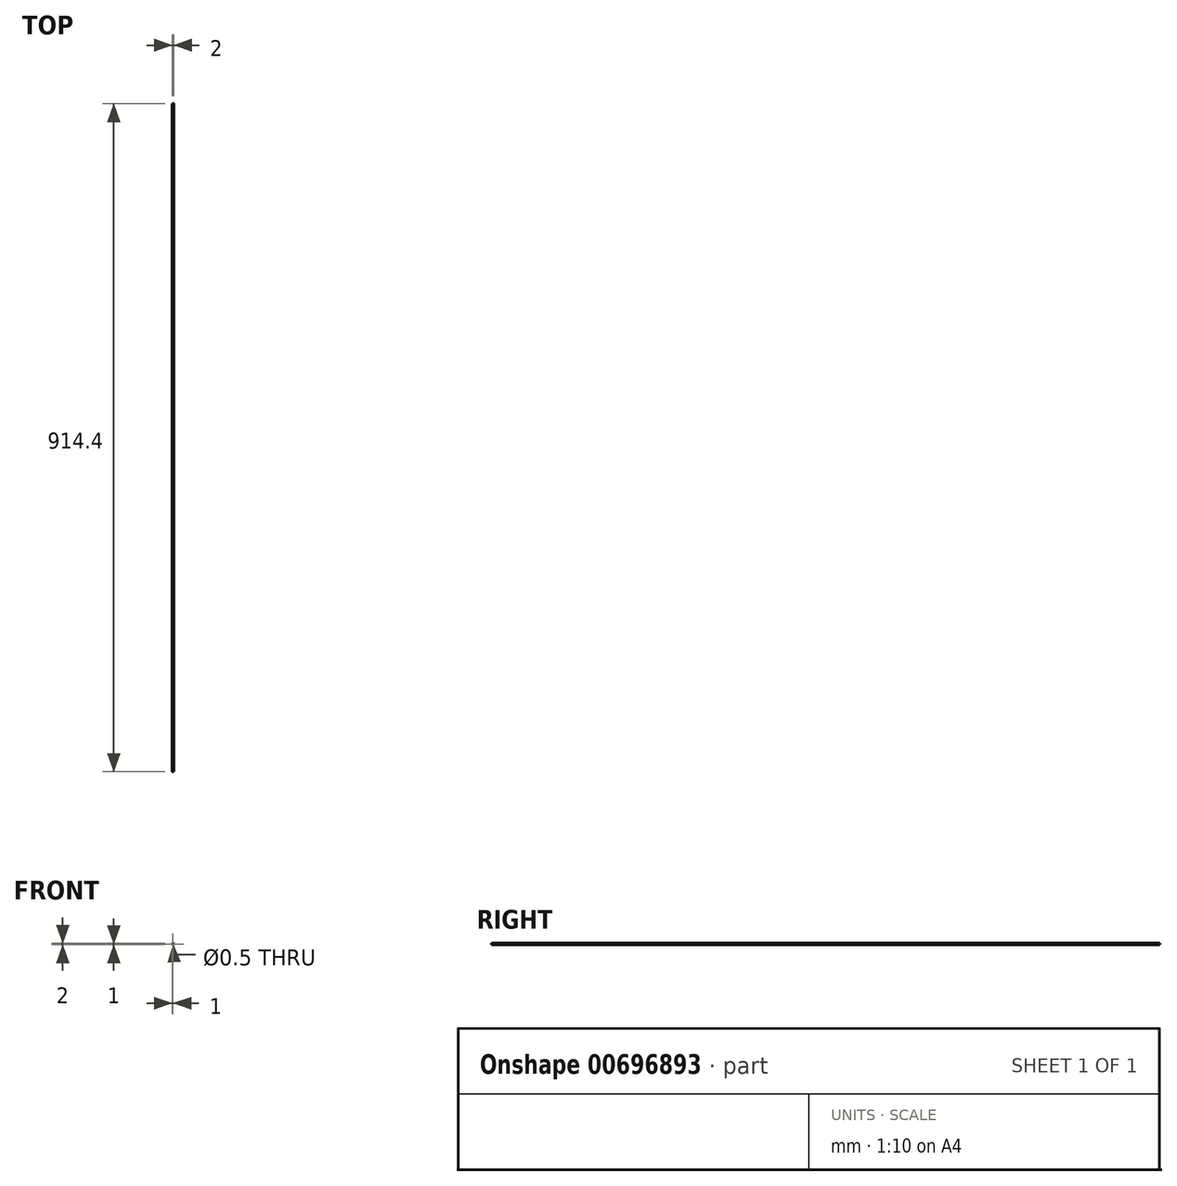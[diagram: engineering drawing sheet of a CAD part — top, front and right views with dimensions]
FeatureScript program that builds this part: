
annotation { "Feature Type Name" : "Feature", "Feature Type Description" : "" }
export const myFeature = defineFeature(function(context is Context, id is Id, definition is map)
    precondition{}
    {
        {
            var Q0;
            Q0=qCreatedBy(makeId("Front.planeOp"),FACE);
            var sketch = newSketch(context, id + "F0", { "sketchPlane" : qUnion([Q0])});
            skCircle(sketch, "E0", {"center": v(0, 0) * mm, "radius": 0.25 * mm});
            skCircle(sketch, "E1", {"center": v(0, 0) * mm, "radius": 1 * mm});
            skSolve(sketch);
        }
        {
            var Q0;
            Q0 = qSketchRegion(id + "F0", true);
            extrude(context, id + "F1", {"entities" : qUnion([Q0]), "depth" : (36 * 25.4) * mm, "offsetDistance" : 25 * mm});
        }
    });
